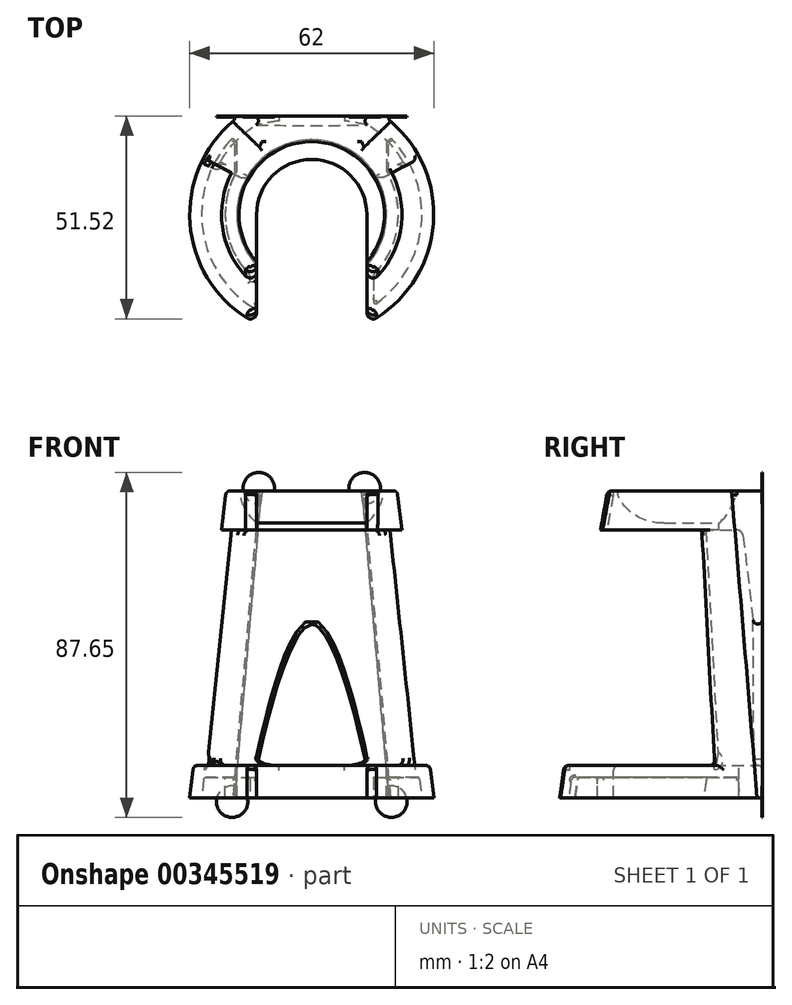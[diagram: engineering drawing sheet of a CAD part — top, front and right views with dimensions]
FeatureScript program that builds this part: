
annotation { "Feature Type Name" : "Feature", "Feature Type Description" : "" }
export const myFeature = defineFeature(function(context is Context, id is Id, definition is map)
    precondition{}
    {
        {
            var Q0;
            Q0=qCreatedBy(makeId("Front.planeOp"),FACE);
            var sketch = newSketch(context, id + "F0", { "sketchPlane" : qUnion([Q0])});
            skLineSegment(sketch, "E0", {"start": v(14, -8.25) * mm, "end": v(14, -10) * mm});
            skLineSegment(sketch, "E1", {"start": v(14, -10) * mm, "end": v(22.91, -10) * mm});
            skLineSegment(sketch, "E2", {"start": v(22.91, -10) * mm, "end": v(21.72, 0) * mm});
            skLineSegment(sketch, "E3", {"start": v(21.72, 0) * mm, "end": v(18.5, 0) * mm});
            skArc(sketch, "E4", {"start": v(14, -8.25) * mm, "mid": v(16.91, -4.49) * mm, "end": v(18.5, 0) * mm});
            skPoint(sketch, "E5.start.orphan", {"position": v(0, -21.84) * mm});
            skLineSegment(sketch, "E6", {"start": v(0, 0) * mm, "end": v(0, -21.84) * mm});
            skLineSegment(sketch, "E7", {"start": v(22.91, -10) * mm, "end": v(31, -78) * mm});
            skLineSegment(sketch, "E8", {"start": v(31, -78) * mm, "end": v(19, -78) * mm});
            skLineSegment(sketch, "E9", {"start": v(19, -78) * mm, "end": v(19, -69.8) * mm});
            skLineSegment(sketch, "E10", {"start": v(19, -69.8) * mm, "end": v(27, -69.8) * mm});
            skLineSegment(sketch, "E11", {"start": v(27, -69.8) * mm, "end": v(19.9, -10) * mm});
            skLineSegment(sketch, "E12", {"start": v(22, -78) * mm, "end": v(22, -72.8) * mm});
            skLineSegment(sketch, "E13", {"start": v(22, -72.8) * mm, "end": v(27.36, -72.8) * mm});
            skLineSegment(sketch, "E14", {"start": v(27.36, -72.8) * mm, "end": v(27.98, -78) * mm});
            skSolve(sketch);
        }
        {
            var Q0;
            {var subQ3=sQuery(id+"F0.wireOp",EDGE,"E0");Q0=makeQuery(id+"F0.imprint","IMPRINT",FACE,{"disambiguationData":[TD([[makeQuery(id+"F0.imprint","IMPRINT",EDGE,{"derivedFrom":subQ3}),1.0]])]});}
            var Q1;
            {var subQ3=sQuery(id+"F0.wireOp",EDGE,"E7");Q1=makeQuery(id+"F0.imprint","IMPRINT",FACE,{"disambiguationData":[TD([[makeQuery(id+"F0.imprint","IMPRINT",EDGE,{"derivedFrom":subQ3}),-1.0]])]});}
            var Q2;
            Q2=sQuery(id+"F0.wireOp",EDGE,"E6");
            revolve(context, id + "F1", {"entities" : qUnion([Q0, Q1]), "axis" : qUnion([Q2]), "revolveType" : RevolveType.FULL});
        }
        {
            var Q0;
            Q0=makeQuery(id+"F1.opRevolve","SWEPT_FACE",FACE,{"disambiguationData":[OSD([sQuery(id+"F0.wireOp",EDGE,"E3")])]});
            var sketch = newSketch(context, id + "F2", { "sketchPlane" : qUnion([Q0])});
            skLineSegment(sketch, "E15.bottom", {"start": v(-14, 0) * mm, "end": v(14, 0) * mm});
            skLineSegment(sketch, "E15.top", {"start": v(-14, -36) * mm, "end": v(14, -36) * mm});
            skLineSegment(sketch, "E15.left", {"start": v(-14, 0) * mm, "end": v(-14, -36) * mm});
            skLineSegment(sketch, "E15.right", {"start": v(14, 0) * mm, "end": v(14, -36) * mm});
            skSolve(sketch);
        }
        {
            var Q0;
            Q0 = qSketchRegion(id + "F2", true);
            extrude(context, id + "F3", {"entities" : qUnion([Q0]), "operationType" : NewBodyOperationType.REMOVE, "endBound" : BoundingType.THROUGH_ALL, "oppositeDirection" : true, "depth" : 25 * mm});
        }
        {
            var Q0;
            Q0=qCreatedBy(makeId("Right.planeOp"),FACE);
            var sketch = newSketch(context, id + "F4", { "sketchPlane" : qUnion([Q0])});
            skLineSegment(sketch, "E16.bottom", {"start": v(0, -10) * mm, "end": v(-34, -10) * mm});
            skLineSegment(sketch, "E16.top", {"start": v(0, -69.8) * mm, "end": v(-34, -69.8) * mm});
            skLineSegment(sketch, "E16.left", {"start": v(0, -10) * mm, "end": v(0, -69.8) * mm});
            skLineSegment(sketch, "E16.right", {"start": v(-34, -10) * mm, "end": v(-34, -69.8) * mm});
            skLineSegment(sketch, "E17", {"start": v(0, 0) * mm, "end": v(0, -10) * mm});
            skSolve(sketch);
        }
        {
            var Q0;
            Q0 = qSketchRegion(id + "F4", true);
            var Q1;
            Q1=sQuery(id+"F4.wireOp",EDGE,"E16.left");
            revolve(context, id + "F5", {"operationType" : NewBodyOperationType.REMOVE, "entities" : qUnion([Q0]), "axis" : qUnion([Q1]), "revolveType" : RevolveType.SYMMETRIC, "angle" : 235 * degree});
        }
        {
            var Q0;
            Q0=qCreatedBy(makeId("Front.planeOp"),FACE);
            cPlane(context, id + "F6", {"entities" : qUnion([Q0]), "cplaneType" : CPlaneType.OFFSET, "offset" : 25 * mm, "oppositeDirection" : true, "width" : 150 * mm, "height" : 150 * mm});
        }
        {
            var Q0;
            Q0=qCreatedBy(id+"F6.planeOp",FACE);
            var sketch = newSketch(context, id + "F7", { "sketchPlane" : qUnion([Q0])});
            skLineSegment(sketch, "E18.bottom", {"start": v(35, 0) * mm, "end": v(-35, 0) * mm});
            skLineSegment(sketch, "E18.top", {"start": v(35, -78) * mm, "end": v(-35, -78) * mm});
            skLineSegment(sketch, "E18.left", {"start": v(35, 0) * mm, "end": v(35, -78) * mm});
            skLineSegment(sketch, "E18.right", {"start": v(-35, 0) * mm, "end": v(-35, -78) * mm});
            skSolve(sketch);
        }
        {
            var Q0;
            Q0 = qSketchRegion(id + "F7", true);
            extrude(context, id + "F8", {"entities" : qUnion([Q0]), "operationType" : NewBodyOperationType.REMOVE, "endBound" : BoundingType.THROUGH_ALL, "oppositeDirection" : true, "depth" : 25 * mm});
        }
        {
            var Q0;
            Q0=qCreatedBy(id+"F6.planeOp",FACE);
            var sketch = newSketch(context, id + "F9", { "sketchPlane" : qUnion([Q0])});
            skLineSegment(sketch, "E19", {"start": v(0, 0) * mm, "end": v(12.7, 0) * mm});
            skLineSegment(sketch, "E20", {"start": v(12.7, 0) * mm, "end": v(19.52, -78) * mm});
            skLineSegment(sketch, "E21", {"start": v(19.52, -78) * mm, "end": v(-19.52, -78) * mm});
            skLineSegment(sketch, "E22", {"start": v(-19.52, -78) * mm, "end": v(-12.7, 0) * mm});
            skLineSegment(sketch, "E23", {"start": v(-12.7, 0) * mm, "end": v(0, 0) * mm});
            skEllipticalArc(sketch, "E24", {});
            skLineSegment(sketch, "E25", {"start": v(15, -72.8) * mm, "end": v(-15, -72.8) * mm});
            skLineSegment(sketch, "E26", {"start": v(0, -32) * mm, "end": v(0, -72.8) * mm});
            skLineSegment(sketch, "E27", {"start": v(-15, -78) * mm, "end": v(-15, -72.8) * mm});
            skLineSegment(sketch, "E28", {"start": v(15, -72.8) * mm, "end": v(15, -78) * mm});
            const initialGuessF9  = {"E24": [0, -0.138, 0, 1, 0.106, 0.019024583716772406, 5.374894592772865, 0.9082907144067219]};
            skSetInitialGuess(sketch, initialGuessF9);
            skSolve(sketch);
        }
        {
            var Q0;
            Q0 = qSketchRegion(id + "F9", true);
            extrude(context, id + "F10", {"entities" : qUnion([Q0]), "operationType" : NewBodyOperationType.ADD, "endBound" : BoundingType.UP_TO_NEXT, "depth" : 25 * mm});
        }
        {
            var Q0;
            {var subQ0=sQuery(id+"F0.wireOp",EDGE,"E9");Q0=makeQuery(id+"F5.boolean.opBoolean","SPLIT",FACE,{"disambiguationData":[TD([makeQuery(id+"F1.opRevolve","SWEPT_FACE",FACE,{"disambiguationData":[OSD([subQ0])]})])],"derivedFrom":makeQuery(id+"F3.boolean.opBoolean","COPY",FACE,{"derivedFrom":makeQuery(id+"F3.opExtrude","SWEPT_FACE",FACE,{"disambiguationData":[OSD([sQuery(id+"F2.wireOp",EDGE,"E15.left")])]})})});}
            var sketch = newSketch(context, id + "F11", { "sketchPlane" : qUnion([Q0])});
            skFitSpline(sketch, "E29.0", {"points": [v(-16.28, -23.3) * mm, v(-17.64, -31.99) * mm, v(-20.23, -49.37) * mm, v(-23.9, -75.48) * mm, v(-27.43, -101.6) * mm, v(-29.73, -119.03) * mm, v(-30.87, -127.74) * mm]});
            skLineSegment(sketch, "E30.0", {"start": v(-16.97, -72.8) * mm, "end": v(-23.5, -72.8) * mm});
            skLineSegment(sketch, "E31.0", {"start": v(-16.97, -78) * mm, "end": v(-16.97, -72.8) * mm});
            skLineSegment(sketch, "E32", {"start": v(-24.22, -78) * mm, "end": v(-16.97, -78) * mm});
            skLineSegment(sketch, "E33", {"start": v(-16.97, -72.8) * mm, "end": v(-14.9, -72.8) * mm});
            skLineSegment(sketch, "E34", {"start": v(-14.9, -72.8) * mm, "end": v(-14.9, -78) * mm});
            skSolve(sketch);
        }
        {
            var Q0;
            Q0 = qSketchRegion(id + "F11", true);
            var Q1;
            {var subQ0=sQuery(id+"F11.wireOp",EDGE,"E31.0");Q1=makeQuery(id+"F11.imprint","IMPRINT",FACE,{"disambiguationData":[TD([[makeQuery(id+"F11.imprint","IMPRINT",EDGE,{"derivedFrom":subQ0}),-1.0]])]});}
            extrude(context, id + "F12", {"entities" : qUnion([Q0, Q1]), "operationType" : NewBodyOperationType.ADD, "oppositeDirection" : true, "depth" : 1.64 * mm});
        }
        {
            var Q0;
            {var subQ0=sQuery(id+"F0.wireOp",EDGE,"E9");Q0=makeQuery(id+"F5.boolean.opBoolean","SPLIT",FACE,{"disambiguationData":[TD([makeQuery(id+"F1.opRevolve","SWEPT_FACE",FACE,{"disambiguationData":[OSD([subQ0])]})])],"derivedFrom":makeQuery(id+"F3.boolean.opBoolean","COPY",FACE,{"derivedFrom":makeQuery(id+"F3.opExtrude","SWEPT_FACE",FACE,{"disambiguationData":[OSD([sQuery(id+"F2.wireOp",EDGE,"E15.right")])]})})});}
            var sketch = newSketch(context, id + "F13", { "sketchPlane" : qUnion([Q0])});
            skLineSegment(sketch, "E35.0", {"start": v(16.97, -78) * mm, "end": v(16.97, -72.8) * mm});
            skLineSegment(sketch, "E36.0", {"start": v(16.97, -72.8) * mm, "end": v(23.5, -72.8) * mm});
            skFitSpline(sketch, "E37.0", {"points": [v(16.28, -23.3) * mm, v(17.64, -31.99) * mm, v(20.23, -49.37) * mm, v(23.9, -75.48) * mm, v(27.43, -101.6) * mm, v(29.73, -119.03) * mm, v(30.87, -127.74) * mm]});
            skLineSegment(sketch, "E38", {"start": v(16.97, -78) * mm, "end": v(24.22, -78) * mm});
            skLineSegment(sketch, "E39", {"start": v(16.97, -78) * mm, "end": v(14.9, -78) * mm});
            skLineSegment(sketch, "E40", {"start": v(14.9, -78) * mm, "end": v(14.9, -72.8) * mm});
            skLineSegment(sketch, "E41", {"start": v(14.9, -72.8) * mm, "end": v(16.97, -72.8) * mm});
            skSolve(sketch);
        }
        {
            var Q0;
            Q0=makeQuery(id+"F13.imprint","IMPRINT",FACE,{"disambiguationData":[TD([[makeQuery(id+"F13.imprint","IMPRINT",EDGE,{"derivedFrom":sQuery(id+"F13.wireOp",EDGE,"E35.0")}),-1.0]])]});
            var Q1;
            Q1=makeQuery(id+"F13.imprint","IMPRINT",FACE,{"disambiguationData":[TD([[makeQuery(id+"F13.imprint","IMPRINT",EDGE,{"derivedFrom":sQuery(id+"F13.wireOp",EDGE,"E35.0")}),1.0]])]});
            extrude(context, id + "F14", {"entities" : qUnion([Q0, Q1]), "operationType" : NewBodyOperationType.ADD, "oppositeDirection" : true, "depth" : 1.64 * mm});
        }
        {
            var Q0;
            {var subQ0=sQuery(id+"F0.wireOp",EDGE,"E13");var subQ1=sQuery(id+"F0.wireOp",EDGE,"E14");Q0=makeQuery(id+"F8.boolean.opBoolean","SPLIT",EDGE,{"disambiguationData":[TD([makeQuery(id+"F3.boolean.opBoolean","COPY",FACE,{"derivedFrom":makeQuery(id+"F3.opExtrude","SWEPT_FACE",FACE,{"disambiguationData":[OSD([sQuery(id+"F2.wireOp",EDGE,"E15.right")])]})})])],"derivedFrom":makeQuery(id+"F1.opRevolve","SWEPT_EDGE",EDGE,{"disambiguationData":[OSD([subQ0,subQ1])]})});}
            var Q1;
            {var subQ1=sQuery(id+"F0.wireOp",EDGE,"E14");Q1=makeQuery(id+"F10.boolean.opBoolean","INTERSECT",EDGE,{"derivedFrom":[makeQuery(id+"F8.boolean.opBoolean","SPLIT",FACE,{"disambiguationData":[TD([makeQuery(id+"F3.boolean.opBoolean","COPY",FACE,{"derivedFrom":makeQuery(id+"F3.opExtrude","SWEPT_FACE",FACE,{"disambiguationData":[OSD([sQuery(id+"F2.wireOp",EDGE,"E15.right")])]})})])],"derivedFrom":makeQuery(id+"F1.opRevolve","SWEPT_FACE",FACE,{"disambiguationData":[OSD([subQ1])]})}),makeQuery(id+"F10.opExtrude","SWEPT_FACE",FACE,{"disambiguationData":[OSD([sQuery(id+"F9.wireOp",EDGE,"E20")])]})]});}
            var Q2;
            Q2=makeQuery(id+"F10.boolean.opBoolean","INTERSECT",EDGE,{"derivedFrom":[makeQuery(id+"F1.opRevolve","SWEPT_FACE",FACE,{"disambiguationData":[OSD([sQuery(id+"F0.wireOp",EDGE,"E13")])]}),makeQuery(id+"F10.opExtrude","SWEPT_FACE",FACE,{"disambiguationData":[OSD([sQuery(id+"F9.wireOp",EDGE,"E20")])]})]});
            var Q3;
            Q3=makeQuery(id+"F10.boolean.opBoolean","INTERSECT",EDGE,{"derivedFrom":[makeQuery(id+"F1.opRevolve","SWEPT_FACE",FACE,{"disambiguationData":[OSD([sQuery(id+"F0.wireOp",EDGE,"E12")])]}),makeQuery(id+"F10.opExtrude","SWEPT_FACE",FACE,{"disambiguationData":[OSD([sQuery(id+"F9.wireOp",EDGE,"E20")])]})]});
            var Q4;
            {var subQ0=sQuery(id+"F0.wireOp",EDGE,"E12");var subQ1=sQuery(id+"F0.wireOp",EDGE,"E13");Q4=makeQuery(id+"F10.boolean.opBoolean","SPLIT",EDGE,{"disambiguationData":[TD([makeQuery(id+"F3.boolean.opBoolean","COPY",FACE,{"derivedFrom":makeQuery(id+"F3.opExtrude","SWEPT_FACE",FACE,{"disambiguationData":[OSD([sQuery(id+"F2.wireOp",EDGE,"E15.right")])]})})])],"derivedFrom":makeQuery(id+"F1.opRevolve","SWEPT_EDGE",EDGE,{"disambiguationData":[OSD([subQ0,subQ1])]})});}
            var Q5;
            Q5=makeQuery(id+"F14.opExtrude","CAP_EDGE",EDGE,{"disambiguationData":[OSD([sQuery(id+"F13.wireOp",EDGE,"E36.0"),sQuery(id+"F13.wireOp",EDGE,"E41")])],"isStart":false});
            var Q6;
            {var subQ1=sQuery(id+"F0.wireOp",EDGE,"E12");Q6=makeQuery(id+"F14.boolean.opBoolean","INTERSECT",EDGE,{"derivedFrom":[makeQuery(id+"F10.boolean.opBoolean","SPLIT",FACE,{"disambiguationData":[TD([makeQuery(id+"F3.boolean.opBoolean","COPY",FACE,{"derivedFrom":makeQuery(id+"F3.opExtrude","SWEPT_FACE",FACE,{"disambiguationData":[OSD([sQuery(id+"F2.wireOp",EDGE,"E15.right")])]})})])],"derivedFrom":makeQuery(id+"F1.opRevolve","SWEPT_FACE",FACE,{"disambiguationData":[OSD([subQ1])]})}),makeQuery(id+"F14.opExtrude","CAP_FACE",FACE,{"disambiguationData":[OSD([sQuery(id+"F13.wireOp",EDGE,"E36.0"),sQuery(id+"F13.wireOp",EDGE,"E37.0"),sQuery(id+"F13.wireOp",EDGE,"E38"),sQuery(id+"F13.wireOp",EDGE,"E39"),sQuery(id+"F13.wireOp",EDGE,"E40"),sQuery(id+"F13.wireOp",EDGE,"E41")])],"isStart":false})]});}
            var Q7;
            {var subQ1=sQuery(id+"F0.wireOp",EDGE,"E14");Q7=makeQuery(id+"F14.boolean.opBoolean","INTERSECT",EDGE,{"derivedFrom":[makeQuery(id+"F8.boolean.opBoolean","SPLIT",FACE,{"disambiguationData":[TD([makeQuery(id+"F3.boolean.opBoolean","COPY",FACE,{"derivedFrom":makeQuery(id+"F3.opExtrude","SWEPT_FACE",FACE,{"disambiguationData":[OSD([sQuery(id+"F2.wireOp",EDGE,"E15.right")])]})})])],"derivedFrom":makeQuery(id+"F1.opRevolve","SWEPT_FACE",FACE,{"disambiguationData":[OSD([subQ1])]})}),makeQuery(id+"F14.opExtrude","CAP_FACE",FACE,{"disambiguationData":[OSD([sQuery(id+"F13.wireOp",EDGE,"E36.0"),sQuery(id+"F13.wireOp",EDGE,"E37.0"),sQuery(id+"F13.wireOp",EDGE,"E38"),sQuery(id+"F13.wireOp",EDGE,"E39"),sQuery(id+"F13.wireOp",EDGE,"E40"),sQuery(id+"F13.wireOp",EDGE,"E41")])],"isStart":false})]});}
            var Q8;
            Q8=makeQuery(id+"F10.boolean.opBoolean","SPLIT",FACE,{"disambiguationData":[TD([makeQuery(id+"F3.boolean.opBoolean","COPY",FACE,{"derivedFrom":makeQuery(id+"F3.opExtrude","SWEPT_FACE",FACE,{"disambiguationData":[OSD([sQuery(id+"F2.wireOp",EDGE,"E15.left")])]})})])],"derivedFrom":makeQuery(id+"F1.opRevolve","SWEPT_FACE",FACE,{"disambiguationData":[OSD([sQuery(id+"F0.wireOp",EDGE,"E13")])]})});
            var Q9;
            {var subQ0=sQuery(id+"F2.wireOp",EDGE,"E15.left");var subQ1=sQuery(id+"F0.wireOp",EDGE,"E8");var subQ2=sQuery(id+"F0.wireOp",EDGE,"E12");Q9=makeQuery(id+"F12.boolean.opBoolean","INTERSECT",EDGE,{"derivedFrom":[makeQuery(id+"F10.boolean.opBoolean","SPLIT",FACE,{"disambiguationData":[TD([makeQuery(id+"F3.boolean.opBoolean","COPY",FACE,{"derivedFrom":makeQuery(id+"F3.opExtrude","SWEPT_FACE",FACE,{"disambiguationData":[OSD([subQ0])]})})])],"derivedFrom":makeQuery(id+"F1.opRevolve","SWEPT_FACE",FACE,{"disambiguationData":[OSD([subQ2])]})}),makeQuery(id+"F12.opExtrude","CAP_FACE",FACE,{"disambiguationData":[OSD([subQ1,subQ0,sQuery(id+"F11.wireOp",EDGE,"E29.0"),sQuery(id+"F11.wireOp",EDGE,"E30.0"),sQuery(id+"F11.wireOp",EDGE,"E32"),sQuery(id+"F11.wireOp",EDGE,"E33"),sQuery(id+"F11.wireOp",EDGE,"E34")])],"isStart":false})]});}
            var Q10;
            Q10=makeQuery(id+"F10.boolean.opBoolean","INTERSECT",EDGE,{"derivedFrom":[makeQuery(id+"F1.opRevolve","SWEPT_FACE",FACE,{"disambiguationData":[OSD([sQuery(id+"F0.wireOp",EDGE,"E12")])]}),makeQuery(id+"F10.opExtrude","SWEPT_FACE",FACE,{"disambiguationData":[OSD([sQuery(id+"F9.wireOp",EDGE,"E22")])]})]});
            var Q11;
            {var subQ1=sQuery(id+"F0.wireOp",EDGE,"E14");Q11=makeQuery(id+"F10.boolean.opBoolean","INTERSECT",EDGE,{"derivedFrom":[makeQuery(id+"F8.boolean.opBoolean","SPLIT",FACE,{"disambiguationData":[TD([makeQuery(id+"F3.boolean.opBoolean","COPY",FACE,{"derivedFrom":makeQuery(id+"F3.opExtrude","SWEPT_FACE",FACE,{"disambiguationData":[OSD([sQuery(id+"F2.wireOp",EDGE,"E15.left")])]})})])],"derivedFrom":makeQuery(id+"F1.opRevolve","SWEPT_FACE",FACE,{"disambiguationData":[OSD([subQ1])]})}),makeQuery(id+"F10.opExtrude","SWEPT_FACE",FACE,{"disambiguationData":[OSD([sQuery(id+"F9.wireOp",EDGE,"E22")])]})]});}
            var Q12;
            {var subQ0=sQuery(id+"F2.wireOp",EDGE,"E15.left");var subQ1=sQuery(id+"F0.wireOp",EDGE,"E8");var subQ2=sQuery(id+"F0.wireOp",EDGE,"E14");Q12=makeQuery(id+"F12.boolean.opBoolean","INTERSECT",EDGE,{"derivedFrom":[makeQuery(id+"F8.boolean.opBoolean","SPLIT",FACE,{"disambiguationData":[TD([makeQuery(id+"F3.boolean.opBoolean","COPY",FACE,{"derivedFrom":makeQuery(id+"F3.opExtrude","SWEPT_FACE",FACE,{"disambiguationData":[OSD([subQ0])]})})])],"derivedFrom":makeQuery(id+"F1.opRevolve","SWEPT_FACE",FACE,{"disambiguationData":[OSD([subQ2])]})}),makeQuery(id+"F12.opExtrude","CAP_FACE",FACE,{"disambiguationData":[OSD([subQ1,subQ0,sQuery(id+"F11.wireOp",EDGE,"E29.0"),sQuery(id+"F11.wireOp",EDGE,"E30.0"),sQuery(id+"F11.wireOp",EDGE,"E32"),sQuery(id+"F11.wireOp",EDGE,"E33"),sQuery(id+"F11.wireOp",EDGE,"E34")])],"isStart":false})]});}
            fillet(context, id + "F15", {"entities" : qUnion([Q0, Q1, Q2, Q3, Q4, Q5, Q6, Q7, Q8, Q9, Q10, Q11, Q12]), "radius" : 0.6 * mm, "tangentPropagation" : true, "allowEdgeOverflow" : false});
        }
        {
            var Q0;
            Q0=makeQuery(id+"F1.opRevolve","SWEPT_EDGE",EDGE,{"disambiguationData":[OSD([sQuery(id+"F0.wireOp",EDGE,"E1"),sQuery(id+"F0.wireOp",EDGE,"E11")])]});
            var Q1;
            {var subQ0=sQuery(id+"F4.wireOp",EDGE,"E16.top");var subQ1=sQuery(id+"F0.wireOp",EDGE,"E11");var subQ2=sQuery(id+"F0.wireOp",EDGE,"E10");Q1=makeQuery(id+"F8.boolean.opBoolean","SPLIT",EDGE,{"disambiguationData":[TD([makeQuery(id+"F5.boolean.opBoolean","COPY",FACE,{"derivedFrom":makeQuery(id+"F5.opRevolve","CAP_FACE",FACE,{"disambiguationData":[OSD([sQuery(id+"F4.wireOp",EDGE,"E16.bottom"),subQ0,sQuery(id+"F4.wireOp",EDGE,"E16.left"),sQuery(id+"F4.wireOp",EDGE,"E16.right")])],"isStart":true})})])],"derivedFrom":makeQuery(id+"F1.opRevolve","SWEPT_EDGE",EDGE,{"disambiguationData":[OSD([subQ2,subQ1])]})});}
            var Q2;
            {var subQ0=sQuery(id+"F4.wireOp",EDGE,"E16.top");var subQ1=sQuery(id+"F0.wireOp",EDGE,"E11");var subQ2=sQuery(id+"F0.wireOp",EDGE,"E10");Q2=makeQuery(id+"F8.boolean.opBoolean","SPLIT",EDGE,{"disambiguationData":[TD([makeQuery(id+"F5.boolean.opBoolean","COPY",FACE,{"derivedFrom":makeQuery(id+"F5.opRevolve","CAP_FACE",FACE,{"disambiguationData":[OSD([sQuery(id+"F4.wireOp",EDGE,"E16.bottom"),subQ0,sQuery(id+"F4.wireOp",EDGE,"E16.left"),sQuery(id+"F4.wireOp",EDGE,"E16.right")])],"isStart":false})})])],"derivedFrom":makeQuery(id+"F1.opRevolve","SWEPT_EDGE",EDGE,{"disambiguationData":[OSD([subQ2,subQ1])]})});}
            var Q3;
            {var subQ0=makeQuery(id+"F3.opExtrude","SWEPT_FACE",FACE,{"disambiguationData":[OSD([sQuery(id+"F2.wireOp",EDGE,"E15.left")])]});var subQ2=sQuery(id+"F0.wireOp",EDGE,"E7");var subQ3=makeQuery(id+"F1.opRevolve","SWEPT_FACE",FACE,{"disambiguationData":[OSD([sQuery(id+"F0.wireOp",EDGE,"E2"),subQ2])]});Q3=makeQuery(id+"F5.boolean.opBoolean","SPLIT",EDGE,{"disambiguationData":[TD([makeQuery(id+"F1.opRevolve","SWEPT_FACE",FACE,{"disambiguationData":[OSD([sQuery(id+"F0.wireOp",EDGE,"E10")])]})])],"derivedFrom":makeQuery(id+"F3.boolean.opBoolean","INTERSECT",EDGE,{"derivedFrom":[subQ3,subQ0]})});}
            var Q4;
            {var subQ0=makeQuery(id+"F3.opExtrude","SWEPT_FACE",FACE,{"disambiguationData":[OSD([sQuery(id+"F2.wireOp",EDGE,"E15.right")])]});var subQ2=sQuery(id+"F0.wireOp",EDGE,"E7");var subQ3=makeQuery(id+"F1.opRevolve","SWEPT_FACE",FACE,{"disambiguationData":[OSD([sQuery(id+"F0.wireOp",EDGE,"E2"),subQ2])]});Q4=makeQuery(id+"F5.boolean.opBoolean","SPLIT",EDGE,{"disambiguationData":[TD([makeQuery(id+"F1.opRevolve","SWEPT_FACE",FACE,{"disambiguationData":[OSD([sQuery(id+"F0.wireOp",EDGE,"E10")])]})])],"derivedFrom":makeQuery(id+"F3.boolean.opBoolean","INTERSECT",EDGE,{"derivedFrom":[subQ3,subQ0]})});}
            var Q5;
            {var subQ0=makeQuery(id+"F3.opExtrude","SWEPT_FACE",FACE,{"disambiguationData":[OSD([sQuery(id+"F2.wireOp",EDGE,"E15.right")])]});var subQ1=makeQuery(id+"F1.opRevolve","SWEPT_FACE",FACE,{"disambiguationData":[OSD([sQuery(id+"F0.wireOp",EDGE,"E2"),sQuery(id+"F0.wireOp",EDGE,"E7")])]});Q5=makeQuery(id+"F5.boolean.opBoolean","SPLIT",EDGE,{"disambiguationData":[TD([makeQuery(id+"F1.opRevolve","SWEPT_FACE",FACE,{"disambiguationData":[OSD([sQuery(id+"F0.wireOp",EDGE,"E1")])]})])],"derivedFrom":makeQuery(id+"F3.boolean.opBoolean","INTERSECT",EDGE,{"derivedFrom":[subQ1,subQ0]})});}
            var Q6;
            {var subQ0=makeQuery(id+"F3.opExtrude","SWEPT_FACE",FACE,{"disambiguationData":[OSD([sQuery(id+"F2.wireOp",EDGE,"E15.left")])]});var subQ1=makeQuery(id+"F1.opRevolve","SWEPT_FACE",FACE,{"disambiguationData":[OSD([sQuery(id+"F0.wireOp",EDGE,"E2"),sQuery(id+"F0.wireOp",EDGE,"E7")])]});Q6=makeQuery(id+"F5.boolean.opBoolean","SPLIT",EDGE,{"disambiguationData":[TD([makeQuery(id+"F1.opRevolve","SWEPT_FACE",FACE,{"disambiguationData":[OSD([sQuery(id+"F0.wireOp",EDGE,"E1")])]})])],"derivedFrom":makeQuery(id+"F3.boolean.opBoolean","INTERSECT",EDGE,{"derivedFrom":[subQ1,subQ0]})});}
            var Q7;
            Q7=makeQuery(id+"F10.boolean.opBoolean","INTERSECT",EDGE,{"derivedFrom":[makeQuery(id+"F1.opRevolve","SWEPT_FACE",FACE,{"disambiguationData":[OSD([sQuery(id+"F0.wireOp",EDGE,"E2"),sQuery(id+"F0.wireOp",EDGE,"E7")])]}),makeQuery(id+"F10.opExtrude","SWEPT_FACE",FACE,{"disambiguationData":[OSD([sQuery(id+"F9.wireOp",EDGE,"E20")])]})]});
            var Q8;
            Q8=makeQuery(id+"F10.boolean.opBoolean","INTERSECT",EDGE,{"derivedFrom":[makeQuery(id+"F1.opRevolve","SWEPT_FACE",FACE,{"disambiguationData":[OSD([sQuery(id+"F0.wireOp",EDGE,"E2"),sQuery(id+"F0.wireOp",EDGE,"E7")])]}),makeQuery(id+"F10.opExtrude","SWEPT_FACE",FACE,{"disambiguationData":[OSD([sQuery(id+"F9.wireOp",EDGE,"E22")])]})]});
            fillet(context, id + "F16", {"entities" : qUnion([Q0, Q1, Q2, Q3, Q4, Q5, Q6, Q7, Q8]), "radius" : 1.6 * mm, "tangentPropagation" : true, "allowEdgeOverflow" : false});
        }
        {
            var Q0;
            Q0=makeQuery(id+"F5.boolean.opBoolean","INTERSECT",EDGE,{"derivedFrom":[makeQuery(id+"F3.boolean.opBoolean","COPY",FACE,{"derivedFrom":makeQuery(id+"F3.opExtrude","SWEPT_FACE",FACE,{"disambiguationData":[OSD([sQuery(id+"F2.wireOp",EDGE,"E15.left")])]})}),makeQuery(id+"F5.opRevolve","SWEPT_FACE",FACE,{"disambiguationData":[OSD([sQuery(id+"F4.wireOp",EDGE,"E16.top")])]})]});
            var Q1;
            Q1=makeQuery(id+"F5.boolean.opBoolean","COPY",EDGE,{"derivedFrom":makeQuery(id+"F5.opRevolve","CAP_EDGE",EDGE,{"disambiguationData":[OSD([sQuery(id+"F4.wireOp",EDGE,"E16.top")])],"isStart":false})});
            var Q2;
            Q2=makeQuery(id+"F5.boolean.opBoolean","INTERSECT",EDGE,{"derivedFrom":[makeQuery(id+"F1.opRevolve","SWEPT_FACE",FACE,{"disambiguationData":[OSD([sQuery(id+"F0.wireOp",EDGE,"E11")])]}),makeQuery(id+"F5.opRevolve","CAP_FACE",FACE,{"disambiguationData":[OSD([sQuery(id+"F4.wireOp",EDGE,"E16.bottom"),sQuery(id+"F4.wireOp",EDGE,"E16.top"),sQuery(id+"F4.wireOp",EDGE,"E16.left"),sQuery(id+"F4.wireOp",EDGE,"E16.right")])],"isStart":false})]});
            var Q3;
            Q3=makeQuery(id+"F5.boolean.opBoolean","INTERSECT",EDGE,{"derivedFrom":[makeQuery(id+"F1.opRevolve","SWEPT_FACE",FACE,{"disambiguationData":[OSD([sQuery(id+"F0.wireOp",EDGE,"E11")])]}),makeQuery(id+"F5.opRevolve","CAP_FACE",FACE,{"disambiguationData":[OSD([sQuery(id+"F4.wireOp",EDGE,"E16.bottom"),sQuery(id+"F4.wireOp",EDGE,"E16.top"),sQuery(id+"F4.wireOp",EDGE,"E16.left"),sQuery(id+"F4.wireOp",EDGE,"E16.right")])],"isStart":true})]});
            var Q4;
            Q4=makeQuery(id+"F5.boolean.opBoolean","INTERSECT",EDGE,{"derivedFrom":[makeQuery(id+"F1.opRevolve","SWEPT_FACE",FACE,{"disambiguationData":[OSD([sQuery(id+"F0.wireOp",EDGE,"E2"),sQuery(id+"F0.wireOp",EDGE,"E7")])]}),makeQuery(id+"F5.opRevolve","CAP_FACE",FACE,{"disambiguationData":[OSD([sQuery(id+"F4.wireOp",EDGE,"E16.bottom"),sQuery(id+"F4.wireOp",EDGE,"E16.top"),sQuery(id+"F4.wireOp",EDGE,"E16.left"),sQuery(id+"F4.wireOp",EDGE,"E16.right")])],"isStart":true})]});
            var Q5;
            Q5=makeQuery(id+"F5.boolean.opBoolean","INTERSECT",EDGE,{"disambiguationData":[OD(0.0)],"derivedFrom":[makeQuery(id+"F1.opRevolve","SWEPT_FACE",FACE,{"disambiguationData":[OSD([sQuery(id+"F0.wireOp",EDGE,"E2"),sQuery(id+"F0.wireOp",EDGE,"E7")])]}),makeQuery(id+"F5.opRevolve","SWEPT_FACE",FACE,{"disambiguationData":[OSD([sQuery(id+"F4.wireOp",EDGE,"E16.top")])]})]});
            var Q6;
            {var subQ0=sQuery(id+"F0.wireOp",EDGE,"E3");var subQ1=sQuery(id+"F0.wireOp",EDGE,"E2");Q6=makeQuery(id+"F10.boolean.opBoolean","SPLIT",EDGE,{"disambiguationData":[TD([makeQuery(id+"F3.boolean.opBoolean","COPY",FACE,{"derivedFrom":makeQuery(id+"F3.opExtrude","SWEPT_FACE",FACE,{"disambiguationData":[OSD([sQuery(id+"F2.wireOp",EDGE,"E15.right")])]})})])],"derivedFrom":makeQuery(id+"F1.opRevolve","SWEPT_EDGE",EDGE,{"disambiguationData":[OSD([subQ1,subQ0])]})});}
            var Q7;
            {var subQ0=sQuery(id+"F0.wireOp",EDGE,"E3");var subQ1=sQuery(id+"F0.wireOp",EDGE,"E2");Q7=makeQuery(id+"F10.boolean.opBoolean","SPLIT",EDGE,{"disambiguationData":[TD([makeQuery(id+"F3.boolean.opBoolean","COPY",FACE,{"derivedFrom":makeQuery(id+"F3.opExtrude","SWEPT_FACE",FACE,{"disambiguationData":[OSD([sQuery(id+"F2.wireOp",EDGE,"E15.left")])]})})])],"derivedFrom":makeQuery(id+"F1.opRevolve","SWEPT_EDGE",EDGE,{"disambiguationData":[OSD([subQ1,subQ0])]})});}
            var Q8;
            Q8=makeQuery(id+"F8.boolean.opBoolean","INTERSECT",EDGE,{"derivedFrom":[makeQuery(id+"F1.opRevolve","SWEPT_FACE",FACE,{"disambiguationData":[OSD([sQuery(id+"F0.wireOp",EDGE,"E11")])]}),makeQuery(id+"F8.opExtrude","CAP_FACE",FACE,{"disambiguationData":[OSD([sQuery(id+"F7.wireOp",EDGE,"E18.bottom"),sQuery(id+"F7.wireOp",EDGE,"E18.top"),sQuery(id+"F7.wireOp",EDGE,"E18.left"),sQuery(id+"F7.wireOp",EDGE,"E18.right")])],"isStart":true})]});
            fillet(context, id + "F17", {"entities" : qUnion([Q0, Q1, Q2, Q3, Q4, Q5, Q6, Q7, Q8]), "radius" : 1.2 * mm, "tangentPropagation" : true, "allowEdgeOverflow" : false});
        }
        {
            var Q0;
            Q0=makeQuery(id+"F10.boolean.opBoolean","MERGE",FACE,{"derivedFrom":[makeQuery(id+"F8.boolean.opBoolean","COPY",FACE,{"derivedFrom":makeQuery(id+"F8.opExtrude","CAP_FACE",FACE,{"disambiguationData":[OSD([sQuery(id+"F7.wireOp",EDGE,"E18.bottom"),sQuery(id+"F7.wireOp",EDGE,"E18.top"),sQuery(id+"F7.wireOp",EDGE,"E18.left"),sQuery(id+"F7.wireOp",EDGE,"E18.right")])],"isStart":true})}),makeQuery(id+"F10.opExtrude","CAP_FACE",FACE,{"disambiguationData":[OSD([sQuery(id+"F9.wireOp",EDGE,"E19"),sQuery(id+"F9.wireOp",EDGE,"E20"),sQuery(id+"F9.wireOp",EDGE,"E21"),sQuery(id+"F9.wireOp",EDGE,"E22"),sQuery(id+"F9.wireOp",EDGE,"E23"),sQuery(id+"F9.wireOp",EDGE,"E24"),sQuery(id+"F9.wireOp",EDGE,"E25")])],"isStart":true})]});
            var sketch = newSketch(context, id + "F18", { "sketchPlane" : qUnion([Q0])});
            skCircle(sketch, "E42", {"center": v(13.45, 0.66) * mm, "radius": 4 * mm});
            skCircle(sketch, "E43", {"center": v(20.23, -78.99) * mm, "radius": 4 * mm});
            skCircle(sketch, "E44.MirrorC", {"center": v(-20.23, -78.99) * mm, "radius": 4 * mm});
            skCircle(sketch, "E45.MirrorC", {"center": v(-13.45, 0.66) * mm, "radius": 4 * mm});
            skSolve(sketch);
        }
        {
            var Q0;
            Q0 = qSketchRegion(id + "F18", true);
            extrude(context, id + "F19", {"entities" : qUnion([Q0]), "operationType" : NewBodyOperationType.ADD, "oppositeDirection" : true, "depth" : 0.2 * mm});
        }
    });
